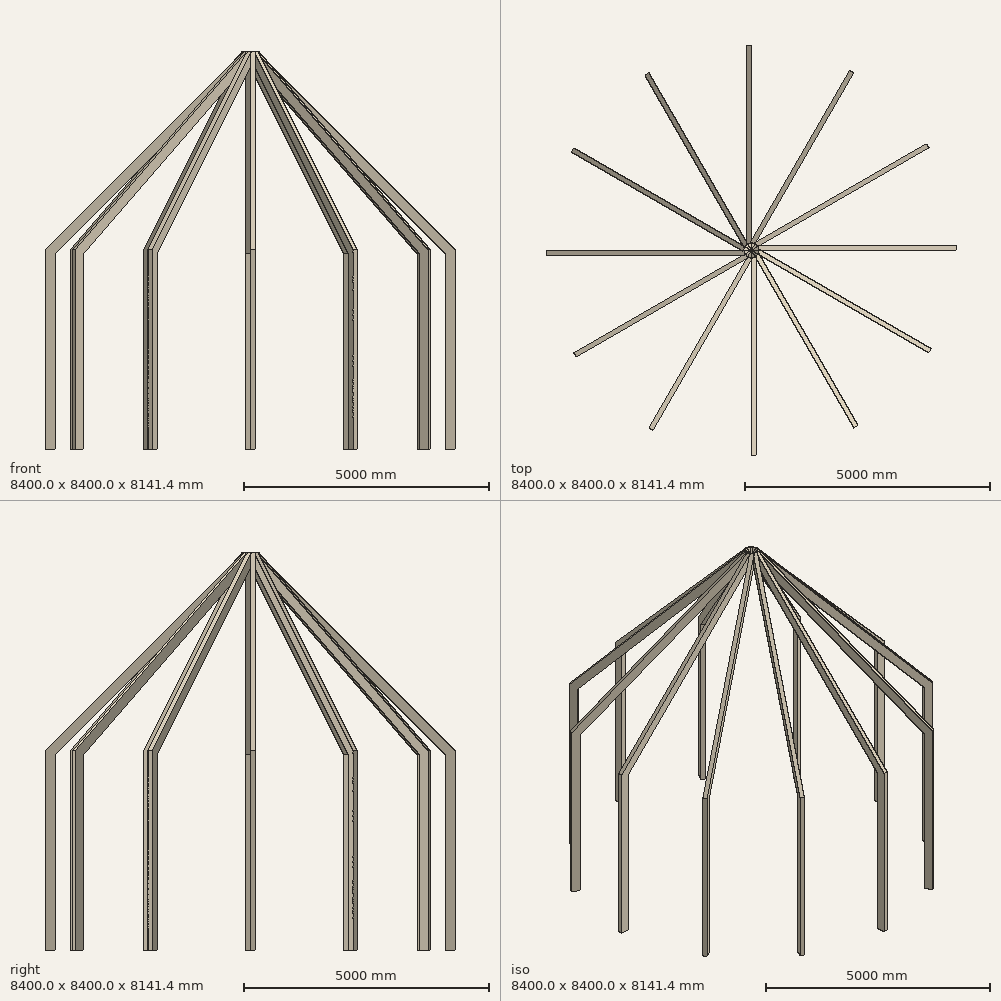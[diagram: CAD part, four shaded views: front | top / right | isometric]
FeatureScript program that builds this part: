
annotation { "Feature Type Name" : "Feature", "Feature Type Description" : "" }
export const myFeature = defineFeature(function(context is Context, id is Id, definition is map)
    precondition{}
    {
        {
            var Q0;
            Q0=qCreatedBy(makeId("Front.planeOp"),FACE);
            var sketch = newSketch(context, id + "F0", { "sketchPlane" : qUnion([Q0])});
            skLineSegment(sketch, "E0", {"start": v(-4000, 0) * mm, "end": v(4000, 0) * mm, "construction": true});
            skLineSegment(sketch, "E1", {"start": v(-4000, 0) * mm, "end": v(-4000, 4000) * mm});
            skLineSegment(sketch, "E2", {"start": v(0, 0) * mm, "end": v(0, 7577.03) * mm, "construction": true});
            skLineSegment(sketch, "E3", {"start": v(-4000, 4000) * mm, "end": v(0, 8000) * mm});
            skLineSegment(sketch, "E4.0", {"start": v(-4200, 4082.84) * mm, "end": v(-141.42, 8141.42) * mm});
            skLineSegment(sketch, "E4.1", {"start": v(-4200, 0) * mm, "end": v(-4200, 4082.84) * mm});
            skLineSegment(sketch, "E5", {"start": v(-141.42, 8141.42) * mm, "end": v(0, 8000) * mm});
            skLineSegment(sketch, "E6", {"start": v(-4200, 0) * mm, "end": v(-4000, 0) * mm});
            skSolve(sketch);
        }
        {
            var Q0;
            Q0 = qSketchRegion(id + "F0", true);
            extrude(context, id + "F1", {"entities" : qUnion([Q0]), "depth" : 100 * mm});
        }
        {
            var Q0;
            Q0=makeQuery(id+"F1.opExtrude","SWEPT_BODY",BODY,{"disambiguationData":[OSD([sQuery(id+"F0.wireOp",EDGE,"E1"),sQuery(id+"F0.wireOp",EDGE,"E3"),sQuery(id+"F0.wireOp",EDGE,"E4.0"),sQuery(id+"F0.wireOp",EDGE,"E4.1"),sQuery(id+"F0.wireOp",EDGE,"E5"),sQuery(id+"F0.wireOp",EDGE,"E6")])]});
            var Q1;
            Q1=sQuery(id+"F0.wireOp",EDGE,"E2");
            circularPattern(context, id + "F2", {"entities" : qUnion([Q0]), "axis" : qUnion([Q1]), "angle" : 360 * degree, "instanceCount" : 12, "equalSpace" : true});
        }
        {
            var Q0;
            Q0=qCreatedBy(makeId("Top.planeOp"),FACE);
            var Q1;
            Q1=sQuery(id+"F0.wireOp",VERTEX,"E3.start");
            cPlane(context, id + "F3", {"entities" : qUnion([Q0, Q1]), "cplaneType" : CPlaneType.PLANE_POINT, "offset" : 25 * mm, "width" : 150 * mm, "height" : 150 * mm});
        }
    });
